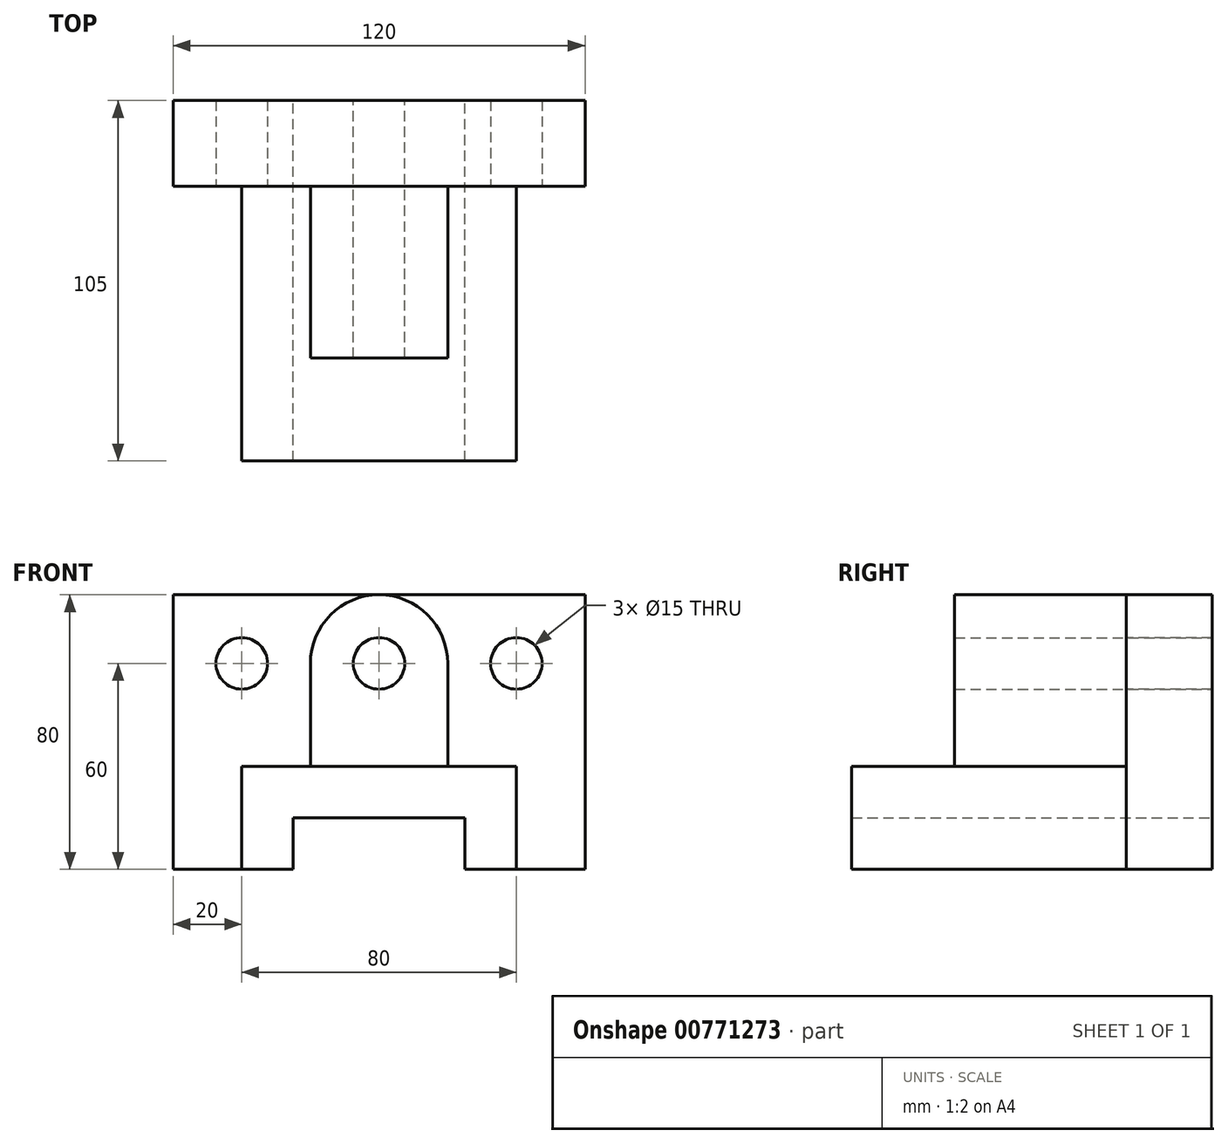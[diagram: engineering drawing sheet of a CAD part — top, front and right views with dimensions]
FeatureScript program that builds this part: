
annotation { "Feature Type Name" : "Feature", "Feature Type Description" : "" }
export const myFeature = defineFeature(function(context is Context, id is Id, definition is map)
    precondition{}
    {
        {
            var Q0;
            Q0=qCreatedBy(makeId("Front.planeOp"),FACE);
            var sketch = newSketch(context, id + "F0", { "sketchPlane" : qUnion([Q0])});
            skLineSegment(sketch, "E0.bottom", {"start": v(0, 0) * mm, "end": v(15, 0) * mm});
            skLineSegment(sketch, "E0.top", {"start": v(0, 30) * mm, "end": v(80, 30) * mm});
            skLineSegment(sketch, "E0.left", {"start": v(0, 0) * mm, "end": v(0, 30) * mm});
            skLineSegment(sketch, "E0.right", {"start": v(80, 0) * mm, "end": v(80, 30) * mm});
            skLineSegment(sketch, "E1", {"start": v(15, 0) * mm, "end": v(15, 15) * mm});
            skLineSegment(sketch, "E2", {"start": v(15, 15) * mm, "end": v(65, 15) * mm});
            skLineSegment(sketch, "E3", {"start": v(65, 15) * mm, "end": v(65, 0) * mm});
            skLineSegment(sketch, "E4", {"start": v(65, 0) * mm, "end": v(80, 0) * mm});
            skSolve(sketch);
        }
        {
            var Q0;
            Q0 = qSketchRegion(id + "F0", true);
            extrude(context, id + "F1", {"entities" : qUnion([Q0]), "depth" : 80 * mm, "offsetDistance" : 25 * mm});
        }
        {
            var Q0;
            Q0=makeQuery(id+"F1.opExtrude","CAP_FACE",FACE,{"disambiguationData":[OSD([sQuery(id+"F0.wireOp",EDGE,"E0.top"),sQuery(id+"F0.wireOp",EDGE,"E0.left"),sQuery(id+"F0.wireOp",EDGE,"E0.right"),sQuery(id+"F0.wireOp",EDGE,"E0.bottom"),sQuery(id+"F0.wireOp",EDGE,"E1"),sQuery(id+"F0.wireOp",EDGE,"E2"),sQuery(id+"F0.wireOp",EDGE,"E3"),sQuery(id+"F0.wireOp",EDGE,"E4")])],"isStart":true});
            var sketch = newSketch(context, id + "F2", { "sketchPlane" : qUnion([Q0])});
            skLineSegment(sketch, "E5", {"start": v(0, 0) * mm, "end": v(20, 0) * mm});
            skLineSegment(sketch, "E6", {"start": v(20, 0) * mm, "end": v(20, 80) * mm});
            skLineSegment(sketch, "E7", {"start": v(20, 80) * mm, "end": v(-100, 80) * mm});
            skLineSegment(sketch, "E8", {"start": v(-100, 80) * mm, "end": v(-100, 0) * mm});
            skLineSegment(sketch, "E9", {"start": v(-100, 0) * mm, "end": v(0, 0) * mm});
            skSolve(sketch);
        }
        {
            var Q0;
            Q0 = qSketchRegion(id + "F2", true);
            extrude(context, id + "F3", {"entities" : qUnion([Q0]), "operationType" : NewBodyOperationType.ADD, "depth" : 25 * mm, "offsetDistance" : 25 * mm});
        }
        {
            var Q0;
            {var subQ0=sQuery(id+"F2.wireOp",EDGE,"E6");var subQ1=sQuery(id+"F2.wireOp",EDGE,"E9");var subQ2=sQuery(id+"F2.wireOp",EDGE,"E5");var subQ3=sQuery(id+"F2.wireOp",EDGE,"E7");var subQ4=sQuery(id+"F2.wireOp",EDGE,"E8");Q0=makeQuery(id+"F3.boolean.opBoolean","SPLIT",FACE,{"disambiguationData":[TD([makeQuery(id+"F1.opExtrude","SWEPT_FACE",FACE,{"disambiguationData":[OSD([sQuery(id+"F0.wireOp",EDGE,"E0.top")])]})])],"derivedFrom":makeQuery(id+"F3.opExtrude","CAP_FACE",FACE,{"disambiguationData":[OSD([subQ2,subQ0,subQ3,subQ4,subQ1])],"isStart":true})});}
            var sketch = newSketch(context, id + "F4", { "sketchPlane" : qUnion([Q0])});
            skLineSegment(sketch, "E10", {"start": v(40, 30) * mm, "end": v(20, 30) * mm});
            skLineSegment(sketch, "E11", {"start": v(20, 30) * mm, "end": v(20, 60) * mm});
            skLineSegment(sketch, "E12", {"start": v(60, 60) * mm, "end": v(60, 30) * mm});
            skLineSegment(sketch, "E13", {"start": v(60, 30) * mm, "end": v(40, 30) * mm});
            skArc(sketch, "E14", {"start": v(60, 60) * mm, "mid": v(40, 80) * mm, "end": v(20, 60) * mm});
            skCircle(sketch, "E15", {"center": v(40, 60) * mm, "radius": 7.5 * mm});
            skSolve(sketch);
        }
        {
            var Q0;
            Q0 = qSketchRegion(id + "F4", true);
            extrude(context, id + "F5", {"entities" : qUnion([Q0]), "operationType" : NewBodyOperationType.ADD, "depth" : 50 * mm, "offsetDistance" : 25 * mm});
        }
        {
            var Q0;
            {var subQ1=makeQuery(id+"F1.opExtrude","SWEPT_FACE",FACE,{"disambiguationData":[OSD([sQuery(id+"F0.wireOp",EDGE,"E0.right")])]});var subQ3=sQuery(id+"F2.wireOp",EDGE,"E7");var subQ5=makeQuery(id+"F1.opExtrude","SWEPT_FACE",FACE,{"disambiguationData":[OSD([sQuery(id+"F0.wireOp",EDGE,"E0.top")])]});var subQ6=sQuery(id+"F2.wireOp",EDGE,"E9");var subQ7=sQuery(id+"F2.wireOp",EDGE,"E8");var subQ8=sQuery(id+"F2.wireOp",EDGE,"E6");var subQ9=sQuery(id+"F2.wireOp",EDGE,"E5");var subQ10=makeQuery(id+"F3.opExtrude","CAP_FACE",FACE,{"disambiguationData":[OSD([subQ9,subQ8,subQ3,subQ7,subQ6])],"isStart":true});Q0=makeQuery(id+"F5.boolean.opBoolean","SPLIT",FACE,{"disambiguationData":[TD([subQ1])],"derivedFrom":makeQuery(id+"F3.boolean.opBoolean","SPLIT",FACE,{"disambiguationData":[TD([subQ5])],"derivedFrom":subQ10})});}
            var sketch = newSketch(context, id + "F6", { "sketchPlane" : qUnion([Q0])});
            skCircle(sketch, "E16", {"center": v(80, 60) * mm, "radius": 7.5 * mm});
            skCircle(sketch, "E17", {"center": v(0, 60) * mm, "radius": 7.5 * mm});
            skPoint(sketch, "E18.orphan", {"position": v(40, 60) * mm});
            skSolve(sketch);
        }
        {
            var Q0;
            Q0 = qSketchRegion(id + "F6", true);
            extrude(context, id + "F7", {"entities" : qUnion([Q0]), "operationType" : NewBodyOperationType.REMOVE, "endBound" : BoundingType.UP_TO_NEXT, "oppositeDirection" : true, "depth" : 25 * mm, "offsetDistance" : 25 * mm});
        }
        {
            var Q0;
            Q0=qCreatedBy(makeId("Right.planeOp"),FACE);
            cPlane(context, id + "F8", {"entities" : qUnion([Q0]), "cplaneType" : CPlaneType.OFFSET, "offset" : 40 * mm, "width" : 150 * mm, "height" : 150 * mm});
        }
        {
            var Q0;
            {var subQ0=sQuery(id+"F2.wireOp",EDGE,"E9");var subQ1=sQuery(id+"F2.wireOp",EDGE,"E5");Q0=makeQuery(id+"F3.boolean.opBoolean","SPLIT",FACE,{"disambiguationData":[TD([makeQuery(id+"F1.opExtrude","SWEPT_FACE",FACE,{"disambiguationData":[OSD([sQuery(id+"F0.wireOp",EDGE,"E1")])]})])],"derivedFrom":makeQuery(id+"F3.opExtrude","CAP_FACE",FACE,{"disambiguationData":[OSD([subQ1,sQuery(id+"F2.wireOp",EDGE,"E6"),sQuery(id+"F2.wireOp",EDGE,"E7"),sQuery(id+"F2.wireOp",EDGE,"E8"),subQ0])],"isStart":true})});}
            var sketch = newSketch(context, id + "F9", { "sketchPlane" : qUnion([Q0])});
            skLineSegment(sketch, "E19.bottom", {"start": v(15, 0) * mm, "end": v(65, 0) * mm});
            skLineSegment(sketch, "E19.top", {"start": v(15, 15) * mm, "end": v(65, 15) * mm});
            skLineSegment(sketch, "E19.left", {"start": v(15, 0) * mm, "end": v(15, 15) * mm});
            skLineSegment(sketch, "E19.right", {"start": v(65, 0) * mm, "end": v(65, 15) * mm});
            skSolve(sketch);
        }
        {
            var Q0;
            Q0 = qSketchRegion(id + "F9", true);
            extrude(context, id + "F10", {"entities" : qUnion([Q0]), "operationType" : NewBodyOperationType.REMOVE, "endBound" : BoundingType.UP_TO_NEXT, "oppositeDirection" : true, "depth" : 25 * mm, "offsetDistance" : 25 * mm});
        }
        {
            var Q0;
            {var subQ0=sQuery(id+"F2.wireOp",EDGE,"E6");var subQ1=sQuery(id+"F2.wireOp",EDGE,"E9");var subQ2=sQuery(id+"F2.wireOp",EDGE,"E5");var subQ3=sQuery(id+"F2.wireOp",EDGE,"E7");var subQ4=sQuery(id+"F2.wireOp",EDGE,"E8");Q0=makeQuery(id+"F5.boolean.opBoolean","SPLIT",FACE,{"disambiguationData":[TD([makeQuery(id+"F5.opExtrude","SWEPT_FACE",FACE,{"disambiguationData":[OSD([sQuery(id+"F4.wireOp",EDGE,"E15")])]})])],"derivedFrom":makeQuery(id+"F3.boolean.opBoolean","SPLIT",FACE,{"disambiguationData":[TD([makeQuery(id+"F1.opExtrude","SWEPT_FACE",FACE,{"disambiguationData":[OSD([sQuery(id+"F0.wireOp",EDGE,"E0.top")])]})])],"derivedFrom":makeQuery(id+"F3.opExtrude","CAP_FACE",FACE,{"disambiguationData":[OSD([subQ2,subQ0,subQ3,subQ4,subQ1])],"isStart":true})})});}
            var sketch = newSketch(context, id + "F11", { "sketchPlane" : qUnion([Q0])});
            skCircle(sketch, "E20", {"center": v(40, 60) * mm, "radius": 7.5 * mm});
            skSolve(sketch);
        }
        {
            var Q0;
            Q0 = qSketchRegion(id + "F11", true);
            extrude(context, id + "F12", {"entities" : qUnion([Q0]), "operationType" : NewBodyOperationType.REMOVE, "endBound" : BoundingType.UP_TO_NEXT, "oppositeDirection" : true, "depth" : 25 * mm, "offsetDistance" : 25 * mm});
        }
    });
